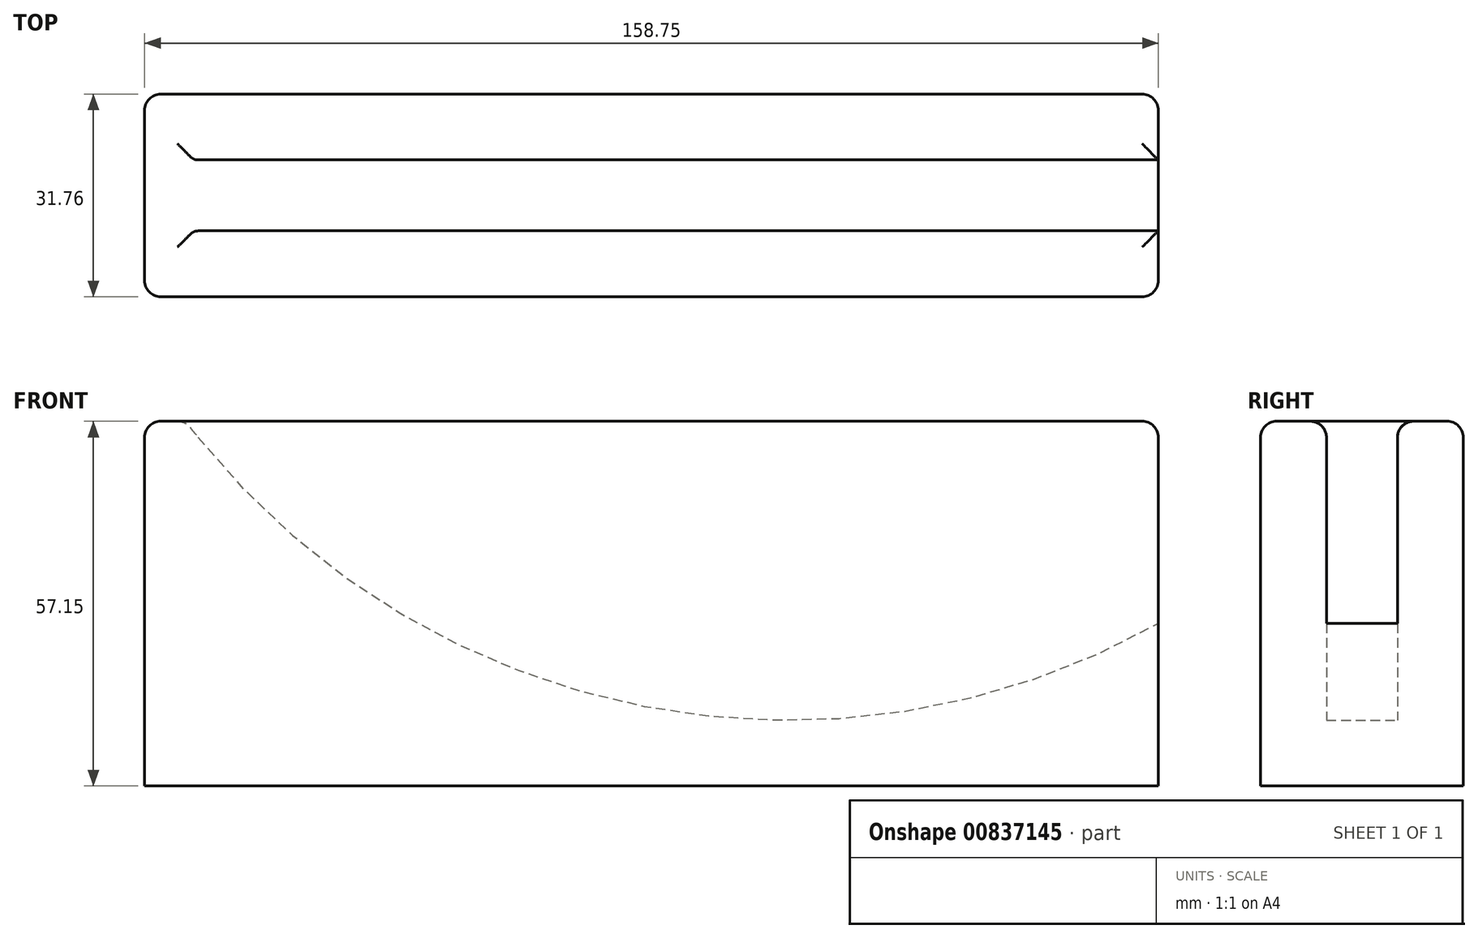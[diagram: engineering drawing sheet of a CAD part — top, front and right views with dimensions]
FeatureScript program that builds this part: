
annotation { "Feature Type Name" : "Feature", "Feature Type Description" : "" }
export const myFeature = defineFeature(function(context is Context, id is Id, definition is map)
    precondition{}
    {
        {
            var Q0;
            Q0=qCreatedBy(makeId("Top.planeOp"),FACE);
            var sketch = newSketch(context, id + "F0", { "sketchPlane" : qUnion([Q0])});
            skLineSegment(sketch, "E0.bottom", {"start": v(-76.2, 15.88) * mm, "end": v(76.2, 15.88) * mm});
            skLineSegment(sketch, "E0.top", {"start": v(-76.2, -15.88) * mm, "end": v(76.2, -15.88) * mm});
            skLineSegment(sketch, "E0.left", {"start": v(-76.2, 15.87) * mm, "end": v(-76.2, -15.88) * mm});
            skLineSegment(sketch, "E0.right", {"start": v(76.2, 15.87) * mm, "end": v(76.2, -15.87) * mm});
            skPoint(sketch, "E1.endSnap0", {"position": v(76.2, 0) * mm});
            skSolve(sketch);
        }
        {
            var Q0;
            Q0=makeQuery(id+"F0.imprint","IMPRINT",FACE,{"disambiguationData":[TD([[makeQuery(id+"F0.imprint","IMPRINT",EDGE,{"derivedFrom":sQuery(id+"F0.wireOp",EDGE,"E0.bottom")}),-1.0]])]});
            extrude(context, id + "F1", {"entities" : qUnion([Q0]), "depth" : 57.15 * mm, "offsetDistance" : 25.4 * mm});
        }
        {
            var Q0;
            Q0=qCreatedBy(makeId("Front.planeOp"),FACE);
            var sketch = newSketch(context, id + "F2", { "sketchPlane" : qUnion([Q0])});
            skLineSegment(sketch, "E2", {"start": v(0, 57.2) * mm, "end": v(-76.2, 57.2) * mm});
            skLineSegment(sketch, "E3", {"start": v(0, 57.2) * mm, "end": v(76.2, 57.2) * mm});
            skLineSegment(sketch, "E4", {"start": v(76.2, 57.2) * mm, "end": v(76.2, 25.46) * mm});
            skArc(sketch, "E5", {"start": v(-76.2, 57.2) * mm, "mid": v(-5.94, 12.81) * mm, "end": v(76.2, 25.46) * mm});
            skSolve(sketch);
        }
        {
            var Q0;
            Q0 = qSketchRegion(id + "F2", true);
            extrude(context, id + "F3", {"entities" : qUnion([Q0]), "operationType" : NewBodyOperationType.REMOVE, "depth" : 5.56 * mm, "offsetDistance" : 25.4 * mm, "hasSecondDirection" : true, "secondDirectionOppositeDirection" : true, "secondDirectionDepth" : 5.56 * mm});
        }
        {
            var Q0;
            Q0=makeQuery(id+"F1.opExtrude","SWEPT_FACE",FACE,{"disambiguationData":[OSD([sQuery(id+"F0.wireOp",EDGE,"E0.left")])]});
            extrude(context, id + "F4", {"entities" : qUnion([Q0]), "operationType" : NewBodyOperationType.ADD, "depth" : 6.35 * mm, "offsetDistance" : 25.4 * mm});
        }
        {
            var Q0;
            {var subQ0=sQuery(id+"F0.wireOp",EDGE,"E0.right");var subQ1=sQuery(id+"F0.wireOp",EDGE,"E0.top");Q0=makeQuery(id+"F3.boolean.opBoolean","SPLIT",EDGE,{"disambiguationData":[TD([makeQuery(id+"F1.opExtrude","SWEPT_FACE",FACE,{"disambiguationData":[OSD([subQ1])]})])],"derivedFrom":makeQuery(id+"F1.opExtrude","CAP_EDGE",EDGE,{"disambiguationData":[OSD([subQ0])],"isStart":false})});}
            var Q1;
            {var subQ0=sQuery(id+"F0.wireOp",EDGE,"E0.left");var subQ1=sQuery(id+"F0.wireOp",EDGE,"E0.top");Q1=makeQuery(id+"F4.boolean.opBoolean","MERGE",EDGE,{"derivedFrom":[makeQuery(id+"F1.opExtrude","CAP_EDGE",EDGE,{"disambiguationData":[OSD([subQ1])],"isStart":false}),makeQuery(id+"F4.opExtrude","SWEPT_EDGE",EDGE,{"disambiguationData":[OSD([subQ1,subQ0]),TDD([makeQuery(id+"F1.opExtrude","CAP_VERTEX",VERTEX,{"disambiguationData":[OSD([subQ1,subQ0])],"isStart":false})])]})]});}
            var Q2;
            Q2=makeQuery(id+"F1.opExtrude","SWEPT_EDGE",EDGE,{"disambiguationData":[OSD([sQuery(id+"F0.wireOp",EDGE,"E0.top"),sQuery(id+"F0.wireOp",EDGE,"E0.right")])]});
            var Q3;
            {var subQ0=sQuery(id+"F0.wireOp",EDGE,"E0.bottom");var subQ1=sQuery(id+"F0.wireOp",EDGE,"E0.right");Q3=makeQuery(id+"F3.boolean.opBoolean","SPLIT",EDGE,{"disambiguationData":[TD([makeQuery(id+"F1.opExtrude","SWEPT_FACE",FACE,{"disambiguationData":[OSD([subQ0])]})])],"derivedFrom":makeQuery(id+"F1.opExtrude","CAP_EDGE",EDGE,{"disambiguationData":[OSD([subQ1])],"isStart":false})});}
            var Q4;
            Q4=makeQuery(id+"F1.opExtrude","SWEPT_EDGE",EDGE,{"disambiguationData":[OSD([sQuery(id+"F0.wireOp",EDGE,"E0.bottom"),sQuery(id+"F0.wireOp",EDGE,"E0.right")])]});
            var Q5;
            {var subQ0=sQuery(id+"F0.wireOp",EDGE,"E0.left");var subQ1=sQuery(id+"F0.wireOp",EDGE,"E0.bottom");Q5=makeQuery(id+"F4.boolean.opBoolean","MERGE",EDGE,{"derivedFrom":[makeQuery(id+"F1.opExtrude","CAP_EDGE",EDGE,{"disambiguationData":[OSD([subQ1])],"isStart":false}),makeQuery(id+"F4.opExtrude","SWEPT_EDGE",EDGE,{"disambiguationData":[OSD([subQ1,subQ0]),TDD([makeQuery(id+"F1.opExtrude","CAP_VERTEX",VERTEX,{"disambiguationData":[OSD([subQ1,subQ0])],"isStart":false})])]})]});}
            var Q6;
            {var subQ0=sQuery(id+"F0.wireOp",EDGE,"E0.left");Q6=makeQuery(id+"F4.opExtrude","CAP_EDGE",EDGE,{"disambiguationData":[OSD([subQ0]),TDD([makeQuery(id+"F1.opExtrude","CAP_EDGE",EDGE,{"disambiguationData":[OSD([subQ0])],"isStart":false})])],"isStart":false});}
            var Q7;
            Q7=makeQuery(id+"F3.boolean.opBoolean","INTERSECT",EDGE,{"derivedFrom":[makeQuery(id+"F1.opExtrude","CAP_FACE",FACE,{"disambiguationData":[OSD([sQuery(id+"F0.wireOp",EDGE,"E0.bottom"),sQuery(id+"F0.wireOp",EDGE,"E0.top"),sQuery(id+"F0.wireOp",EDGE,"E0.left"),sQuery(id+"F0.wireOp",EDGE,"E0.right")])],"isStart":false}),makeQuery(id+"F3.opExtrude","CAP_FACE",FACE,{"disambiguationData":[OSD([sQuery(id+"F2.wireOp",EDGE,"E2"),sQuery(id+"F2.wireOp",EDGE,"E3"),sQuery(id+"F2.wireOp",EDGE,"E4"),sQuery(id+"F2.wireOp",EDGE,"E5")])],"isStart":false})]});
            var Q8;
            Q8=makeQuery(id+"F3.boolean.opBoolean","INTERSECT",EDGE,{"derivedFrom":[makeQuery(id+"F1.opExtrude","CAP_FACE",FACE,{"disambiguationData":[OSD([sQuery(id+"F0.wireOp",EDGE,"E0.bottom"),sQuery(id+"F0.wireOp",EDGE,"E0.top"),sQuery(id+"F0.wireOp",EDGE,"E0.left"),sQuery(id+"F0.wireOp",EDGE,"E0.right")])],"isStart":false}),makeQuery(id+"F3.opExtrude","SWEPT_FACE",FACE,{"disambiguationData":[OSD([sQuery(id+"F2.wireOp",EDGE,"E5")])]})]});
            var Q9;
            Q9=makeQuery(id+"F3.boolean.opBoolean","INTERSECT",EDGE,{"derivedFrom":[makeQuery(id+"F1.opExtrude","CAP_FACE",FACE,{"disambiguationData":[OSD([sQuery(id+"F0.wireOp",EDGE,"E0.bottom"),sQuery(id+"F0.wireOp",EDGE,"E0.top"),sQuery(id+"F0.wireOp",EDGE,"E0.left"),sQuery(id+"F0.wireOp",EDGE,"E0.right")])],"isStart":false}),makeQuery(id+"F3.opExtrude","CAP_FACE",FACE,{"disambiguationData":[OSD([sQuery(id+"F2.wireOp",EDGE,"E2"),sQuery(id+"F2.wireOp",EDGE,"E3"),sQuery(id+"F2.wireOp",EDGE,"E4"),sQuery(id+"F2.wireOp",EDGE,"E5")])],"isStart":true})]});
            var Q10;
            Q10=makeQuery(id+"F3.boolean.opBoolean","COPY",EDGE,{"derivedFrom":makeQuery(id+"F3.opExtrude","CAP_EDGE",EDGE,{"disambiguationData":[OSD([sQuery(id+"F2.wireOp",EDGE,"E4")])],"isStart":true})});
            var Q11;
            Q11=makeQuery(id+"F3.boolean.opBoolean","COPY",EDGE,{"derivedFrom":makeQuery(id+"F3.opExtrude","CAP_EDGE",EDGE,{"disambiguationData":[OSD([sQuery(id+"F2.wireOp",EDGE,"E4")])],"isStart":false})});
            var Q12;
            Q12=makeQuery(id+"F3.boolean.opBoolean","COPY",EDGE,{"derivedFrom":makeQuery(id+"F3.opExtrude","SWEPT_EDGE",EDGE,{"disambiguationData":[OSD([sQuery(id+"F2.wireOp",EDGE,"E4"),sQuery(id+"F2.wireOp",EDGE,"E5")])]})});
            fillet(context, id + "F5", {"entities" : qUnion([Q0, Q1, Q2, Q3, Q4, Q5, Q6, Q7, Q8, Q9, Q10, Q11, Q12]), "radius" : 2.54 * mm, "tangentPropagation" : true, "allowEdgeOverflow" : false});
        }
        {
            var Q0;
            Q0=makeQuery(id+"F4.opExtrude","CAP_EDGE",EDGE,{"disambiguationData":[OSD([sQuery(id+"F0.wireOp",EDGE,"E0.bottom"),sQuery(id+"F0.wireOp",EDGE,"E0.left")])],"isStart":false});
            var Q1;
            Q1=makeQuery(id+"F4.opExtrude","CAP_EDGE",EDGE,{"disambiguationData":[OSD([sQuery(id+"F0.wireOp",EDGE,"E0.top"),sQuery(id+"F0.wireOp",EDGE,"E0.left")])],"isStart":false});
            fillet(context, id + "F6", {"entities" : qUnion([Q0, Q1]), "radius" : 2.54 * mm, "tangentPropagation" : true, "allowEdgeOverflow" : false});
        }
    });
